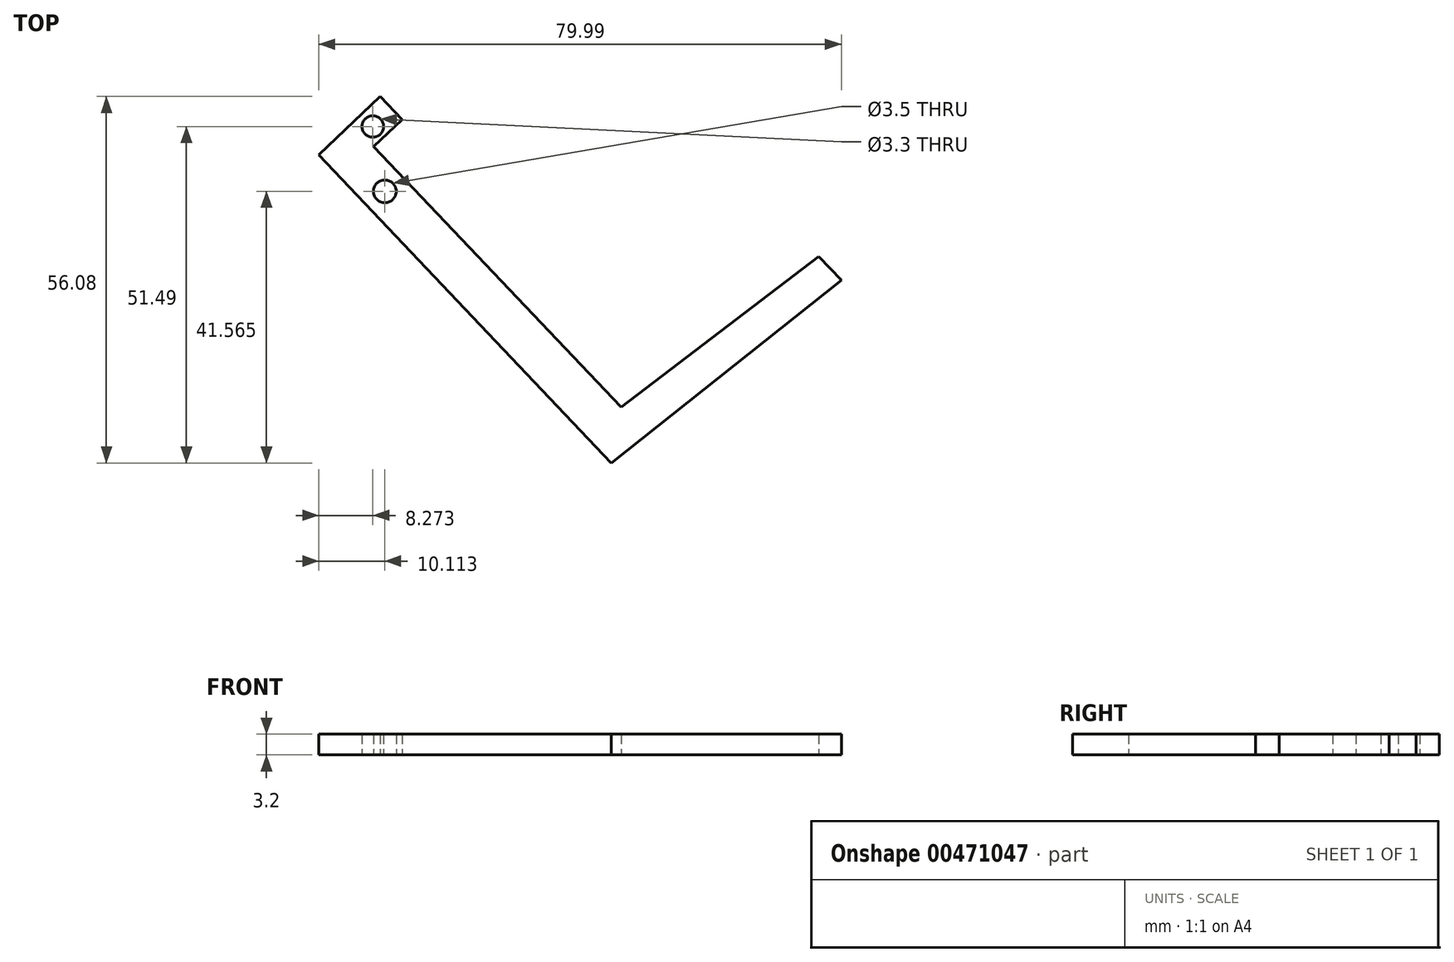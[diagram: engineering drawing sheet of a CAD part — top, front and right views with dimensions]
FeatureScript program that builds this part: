
annotation { "Feature Type Name" : "Feature", "Feature Type Description" : "" }
export const myFeature = defineFeature(function(context is Context, id is Id, definition is map)
    precondition{}
    {
        {
            var Q0;
            Q0=qCreatedBy(makeId("Top.planeOp"),FACE);
            var sketch = newSketch(context, id + "F0", { "sketchPlane" : qUnion([Q0])});
            skLineSegment(sketch, "E0", {"start": v(107.06, -32.64) * mm, "end": v(71.83, -60.63) * mm});
            skLineSegment(sketch, "E1", {"start": v(71.83, -60.63) * mm, "end": v(27.07, -13.5) * mm});
            skLineSegment(sketch, "E2", {"start": v(27.07, -13.5) * mm, "end": v(36.5, -4.55) * mm});
            skLineSegment(sketch, "E3", {"start": v(36.5, -4.55) * mm, "end": v(39.83, -8.05) * mm});
            skLineSegment(sketch, "E4", {"start": v(39.83, -8.05) * mm, "end": v(35.48, -12.19) * mm});
            skLineSegment(sketch, "E5", {"start": v(35.48, -12.19) * mm, "end": v(73.35, -52.07) * mm});
            skLineSegment(sketch, "E6", {"start": v(73.35, -52.07) * mm, "end": v(103.58, -29.05) * mm});
            skCircle(sketch, "E7", {"center": v(37.18, -19.07) * mm, "radius": 1.75 * mm});
            skCircle(sketch, "E8", {"center": v(35.34, -9.14) * mm, "radius": 1.65 * mm});
            skLineSegment(sketch, "E9", {"start": v(103.58, -29.05) * mm, "end": v(107.06, -32.64) * mm});
            skSolve(sketch);
        }
        {
            var Q0;
            Q0 = qSketchRegion(id + "F0", true);
            extrude(context, id + "F1", {"entities" : qUnion([Q0]), "depth" : 3.2 * mm, "offsetDistance" : 25 * mm});
        }
    });
